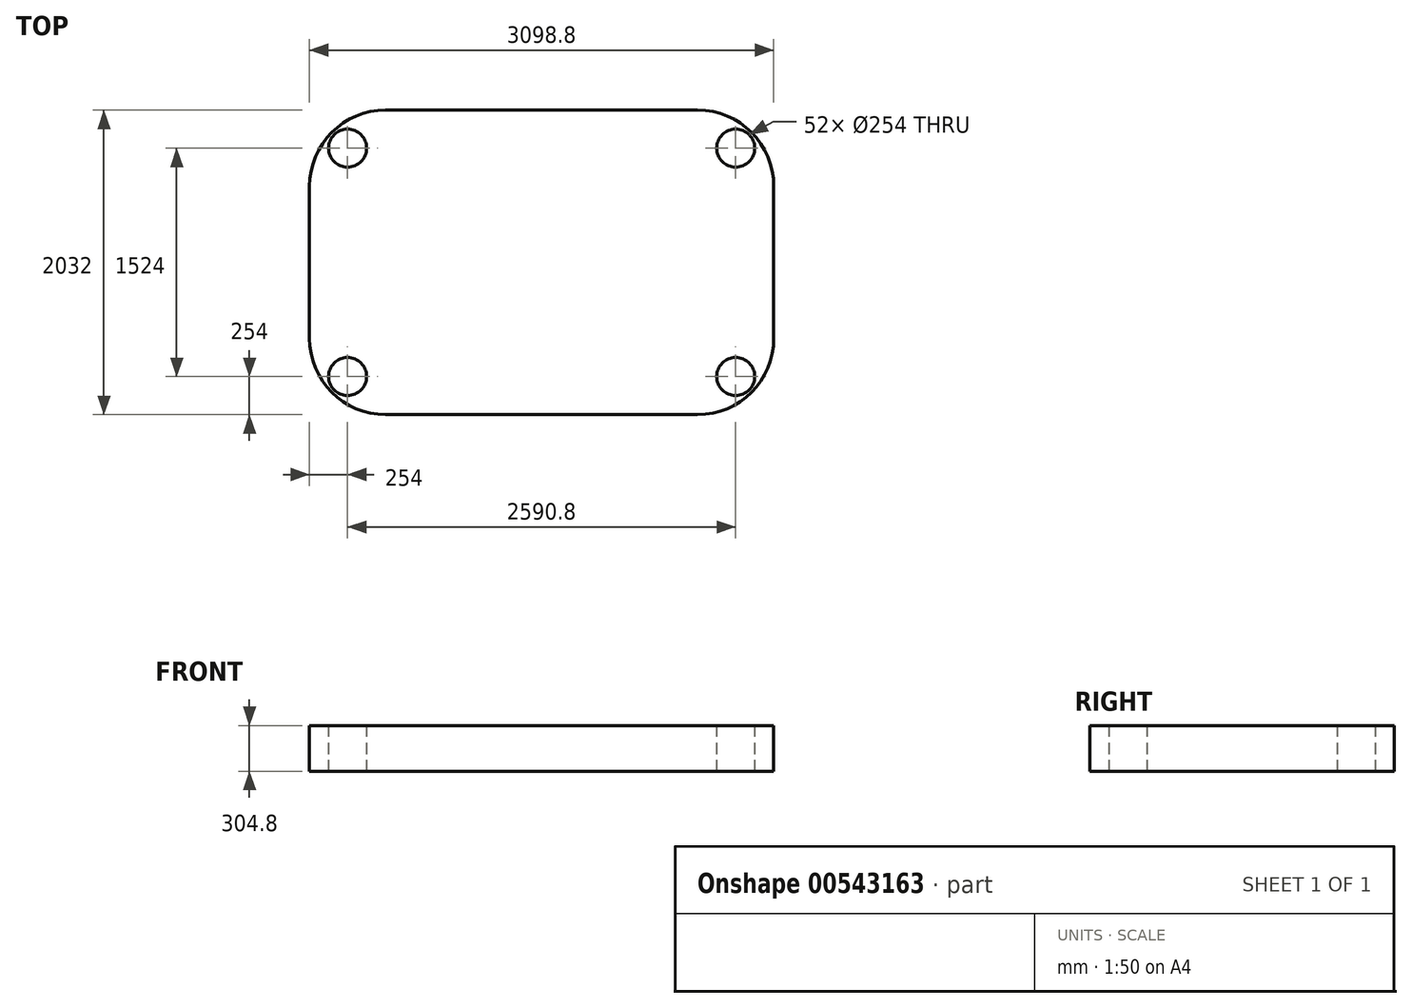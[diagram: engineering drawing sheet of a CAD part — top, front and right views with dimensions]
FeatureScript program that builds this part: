
annotation { "Feature Type Name" : "Feature", "Feature Type Description" : "" }
export const myFeature = defineFeature(function(context is Context, id is Id, definition is map)
    precondition{}
    {
        {
            var Q0;
            Q0=qCreatedBy(makeId("Top.planeOp"),FACE);
            var sketch = newSketch(context, id + "F0", { "sketchPlane" : qUnion([Q0])});
            skLineSegment(sketch, "E0.bottom", {"start": v(1549.4, 1016) * mm, "end": v(-1549.4, 1016) * mm});
            skLineSegment(sketch, "E0.top", {"start": v(1549.4, -1016) * mm, "end": v(-1549.4, -1016) * mm});
            skLineSegment(sketch, "E0.left", {"start": v(1549.4, 1016) * mm, "end": v(1549.4, -1016) * mm});
            skLineSegment(sketch, "E0.right", {"start": v(-1549.4, 1016) * mm, "end": v(-1549.4, -1016) * mm});
            skPoint(sketch, "E0.middle", {"position": v(0, 0) * mm});
            skCircle(sketch, "E1", {"center": v(1295.4, -762) * mm, "radius": 127 * mm});
            skCircle(sketch, "E2", {"center": v(1295.4, 762) * mm, "radius": 127 * mm});
            skCircle(sketch, "E3", {"center": v(-1295.4, 762) * mm, "radius": 127 * mm});
            skCircle(sketch, "E4", {"center": v(-1295.4, -762) * mm, "radius": 127 * mm});
            skSolve(sketch);
        }
        {
            var Q0;
            Q0=makeQuery(id+"F0.imprint","IMPRINT",FACE,{"disambiguationData":[TD([[makeQuery(id+"F0.imprint","IMPRINT",EDGE,{"derivedFrom":sQuery(id+"F0.wireOp",EDGE,"E0.bottom")}),1.0]])]});
            extrude(context, id + "F1", {"entities" : qUnion([Q0]), "depth" : 304.8 * mm, "offsetDistance" : 25.4 * mm});
        }
        {
            var Q0;
            Q0=makeQuery(id+"F1.opExtrude","SWEPT_EDGE",EDGE,{"disambiguationData":[OSD([sQuery(id+"F0.wireOp",EDGE,"E0.bottom"),sQuery(id+"F0.wireOp",EDGE,"E0.left")])]});
            var Q1;
            Q1=makeQuery(id+"F1.opExtrude","SWEPT_EDGE",EDGE,{"disambiguationData":[OSD([sQuery(id+"F0.wireOp",EDGE,"E0.top"),sQuery(id+"F0.wireOp",EDGE,"E0.left")])]});
            var Q2;
            Q2=makeQuery(id+"F1.opExtrude","SWEPT_EDGE",EDGE,{"disambiguationData":[OSD([sQuery(id+"F0.wireOp",EDGE,"E0.bottom"),sQuery(id+"F0.wireOp",EDGE,"E0.right")])]});
            var Q3;
            Q3=makeQuery(id+"F1.opExtrude","SWEPT_EDGE",EDGE,{"disambiguationData":[OSD([sQuery(id+"F0.wireOp",EDGE,"E0.top"),sQuery(id+"F0.wireOp",EDGE,"E0.right")])]});
            fillet(context, id + "F2", {"entities" : qUnion([Q0, Q1, Q2, Q3]), "radius" : 508 * mm, "tangentPropagation" : true, "allowEdgeOverflow" : false});
        }
    });
